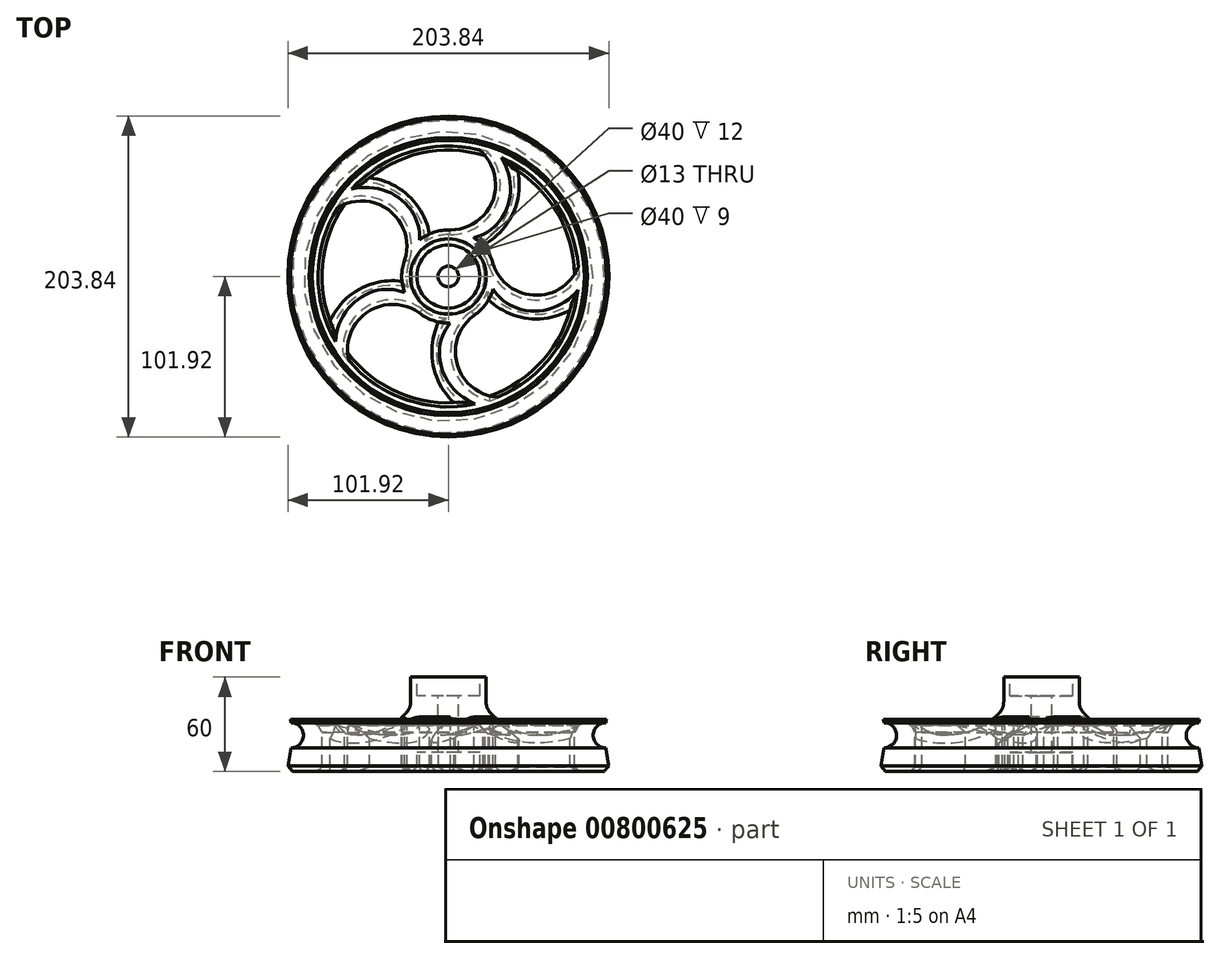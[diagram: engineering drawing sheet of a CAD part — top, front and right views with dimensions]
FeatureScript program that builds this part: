
annotation { "Feature Type Name" : "Feature", "Feature Type Description" : "" }
export const myFeature = defineFeature(function(context is Context, id is Id, definition is map)
    precondition{}
    {
        {
            var Q0;
            Q0=qCreatedBy(makeId("Front.planeOp"),FACE);
            var sketch = newSketch(context, id + "F0", { "sketchPlane" : qUnion([Q0])});
            skArc(sketch, "E0", {"start": v(100, 8) * mm, "mid": v(92, 0) * mm, "end": v(100, -8) * mm});
            skLineSegment(sketch, "E1", {"start": v(125.58, -23) * mm, "end": v(0, -23) * mm, "construction": true});
            skLineSegment(sketch, "E2", {"start": v(102.5, -11.93) * mm, "end": v(102.5, -49.99) * mm, "construction": true});
            skLineSegment(sketch, "E3", {"start": v(100, -8) * mm, "end": v(102.5, -23) * mm});
            skLineSegment(sketch, "E4.MirrorCS", {"start": v(100, 8) * mm, "end": v(100.33, 10) * mm});
            skPoint(sketch, "E5.orphan", {"position": v(102.5, 23) * mm});
            skLineSegment(sketch, "E6", {"start": v(102.5, -23) * mm, "end": v(92.5, -23) * mm});
            skArc(sketch, "E7", {"start": v(88.37, 10) * mm, "mid": v(87.38, 9.33) * mm, "end": v(86.46, 8.57) * mm});
            skLineSegment(sketch, "E8", {"start": v(100.33, 10) * mm, "end": v(88.37, 10) * mm});
            skLineSegment(sketch, "E9", {"start": v(0, 37) * mm, "end": v(98, 37) * mm, "construction": true});
            skLineSegment(sketch, "E10", {"start": v(20, 37) * mm, "end": v(20, 25) * mm});
            skLineSegment(sketch, "E11", {"start": v(20, 25) * mm, "end": v(6.5, 25) * mm});
            skLineSegment(sketch, "E12", {"start": v(6.5, 25) * mm, "end": v(6.5, -11) * mm});
            skLineSegment(sketch, "E13", {"start": v(6.5, -11) * mm, "end": v(20, -11) * mm});
            skLineSegment(sketch, "E14", {"start": v(20, 37) * mm, "end": v(0, 37) * mm});
            skLineSegment(sketch, "E15", {"start": v(0, -23) * mm, "end": v(20, -23) * mm});
            skLineSegment(sketch, "E16.trimOffspring", {"start": v(20, -11) * mm, "end": v(20, -23) * mm});
            skLineSegment(sketch, "E17", {"start": v(20, 37) * mm, "end": v(24, 37) * mm});
            skLineSegment(sketch, "E18", {"start": v(24, 37) * mm, "end": v(24, 17.35) * mm});
            skLineSegment(sketch, "E19", {"start": v(24, -23) * mm, "end": v(20, -23) * mm});
            skLineSegment(sketch, "E20", {"start": v(24, -23) * mm, "end": v(92.5, -23) * mm});
            skArc(sketch, "E21", {"start": v(24, 17.35) * mm, "mid": v(54.67, 0.42) * mm, "end": v(88.37, 10) * mm});
            skLineSegment(sketch, "E22", {"start": v(0, 51.8) * mm, "end": v(0, -76.47) * mm, "construction": true});
            skSolve(sketch);
        }
        {
            var Q0;
            Q0 = qSketchRegion(id + "F0", true);
            var Q1;
            Q1=sQuery(id+"F0.wireOp",EDGE,"E22");
            revolve(context, id + "F1", {"surfaceOperationType" : NewSurfaceOperationType.NEW, "entities" : qUnion([Q0]), "axis" : qUnion([Q1]), "revolveType" : RevolveType.FULL});
        }
        {
            var Q0;
            Q0=makeQuery(id+"F1.opRevolve","SWEPT_FACE",FACE,{"disambiguationData":[OSD([sQuery(id+"F0.wireOp",EDGE,"E17")])]});
            var sketch = newSketch(context, id + "F2", { "sketchPlane" : qUnion([Q0])});
            skCircle(sketch, "E23", {"center": v(0, 0) * mm, "radius": 29.57 * mm});
            skCircle(sketch, "E24", {"center": v(0, 0) * mm, "radius": 80.24 * mm});
            skArc(sketch, "E25", {"start": v(0, 29.57) * mm, "mid": v(27.05, 45.57) * mm, "end": v(23.32, 76.77) * mm});
            skArc(sketch, "E26.0", {"start": v(22, 19.77) * mm, "mid": v(40.88, 39.72) * mm, "end": v(44.15, 67) * mm});
            skArc(sketch, "E27.1.0", {"start": v(-28.12, 9.14) * mm, "mid": v(-34.98, 39.8) * mm, "end": v(-65.81, 45.9) * mm});
            skArc(sketch, "E27.1.1", {"start": v(-12, 27.02) * mm, "mid": v(-25.14, 51.15) * mm, "end": v(-50.07, 62.7) * mm});
            skArc(sketch, "E27.2.0", {"start": v(-17.38, -23.92) * mm, "mid": v(-48.67, -20.97) * mm, "end": v(-64, -48.4) * mm});
            skArc(sketch, "E27.2.1", {"start": v(-29.41, -3.06) * mm, "mid": v(-56.42, -8.1) * mm, "end": v(-75.1, -28.25) * mm});
            skArc(sketch, "E27.3.0", {"start": v(17.38, -23.92) * mm, "mid": v(4.9, -52.77) * mm, "end": v(26.26, -75.82) * mm});
            skArc(sketch, "E27.3.1", {"start": v(-6.17, -28.92) * mm, "mid": v(-9.73, -56.16) * mm, "end": v(3.66, -80.15) * mm});
            skArc(sketch, "E27.4.0", {"start": v(28.12, 9.14) * mm, "mid": v(51.7, -11.64) * mm, "end": v(80.22, 1.55) * mm});
            skArc(sketch, "E27.4.1", {"start": v(25.6, -14.8) * mm, "mid": v(50.4, -26.6) * mm, "end": v(77.36, -21.3) * mm});
            skSolve(sketch);
        }
        {
            var Q0;
            {var subQ6=sQuery(id+"F2.wireOp",EDGE,"E27.2.1");Q0=makeQuery(id+"F2.imprint","IMPRINT",FACE,{"disambiguationData":[TD([[makeQuery(id+"F2.imprint","IMPRINT",EDGE,{"derivedFrom":subQ6}),-1.0]])]});}
            var Q1;
            {var subQ6=sQuery(id+"F2.wireOp",EDGE,"E27.1.1");Q1=makeQuery(id+"F2.imprint","IMPRINT",FACE,{"disambiguationData":[TD([[makeQuery(id+"F2.imprint","IMPRINT",EDGE,{"derivedFrom":subQ6}),-1.0]])]});}
            var Q2;
            {var subQ0=sQuery(id+"F2.wireOp",EDGE,"E26.0");Q2=makeQuery(id+"F2.imprint","IMPRINT",FACE,{"disambiguationData":[TD([[makeQuery(id+"F2.imprint","IMPRINT",EDGE,{"derivedFrom":subQ0}),-1.0]])]});}
            var Q3;
            {var subQ6=sQuery(id+"F2.wireOp",EDGE,"E27.4.1");Q3=makeQuery(id+"F2.imprint","IMPRINT",FACE,{"disambiguationData":[TD([[makeQuery(id+"F2.imprint","IMPRINT",EDGE,{"derivedFrom":subQ6}),-1.0]])]});}
            var Q4;
            {var subQ5=sQuery(id+"F2.wireOp",EDGE,"E27.3.1");Q4=makeQuery(id+"F2.imprint","IMPRINT",FACE,{"disambiguationData":[TD([[makeQuery(id+"F2.imprint","IMPRINT",EDGE,{"derivedFrom":subQ5}),-1.0]])]});}
            extrude(context, id + "F3", {"entities" : qUnion([Q0, Q1, Q2, Q3, Q4]), "operationType" : NewBodyOperationType.REMOVE, "endBound" : BoundingType.THROUGH_ALL, "oppositeDirection" : true, "depth" : 25 * mm, "offsetDistance" : 25 * mm});
        }
        {
            var Q0;
            Q0=makeQuery(id+"F1.opRevolve","SWEPT_FACE",FACE,{"disambiguationData":[OSD([sQuery(id+"F0.wireOp",EDGE,"E6"),sQuery(id+"F0.wireOp",EDGE,"E19"),sQuery(id+"F0.wireOp",EDGE,"E20")])]});
            chamfer(context, id + "F4", {"entities" : qUnion([Q0]), "width" : 3 * mm, "tangentPropagation" : true});
        }
        {
            var Q0;
            {var subQ0=sQuery(id+"F2.wireOp",EDGE,"E24");Q0=makeQuery(id+"F3.boolean.opBoolean","INTERSECT",EDGE,{"derivedFrom":[makeQuery(id+"F1.opRevolve","SWEPT_FACE",FACE,{"disambiguationData":[OSD([sQuery(id+"F0.wireOp",EDGE,"E21")])]}),makeQuery(id+"F3.opExtrude","SWEPT_FACE",FACE,{"disambiguationData":[OSD([subQ0]),TDD([makeQuery(id+"F2.imprint","IMPRINT",EDGE,{"disambiguationData":[TD([[makeQuery(id+"F2.imprint","INTERSECT",VERTEX,{"derivedFrom":[subQ0,sQuery(id+"F2.wireOp",EDGE,"E25")]}),-1.0]])],"derivedFrom":subQ0})])]})]});}
            var Q1;
            {var subQ0=sQuery(id+"F2.wireOp",EDGE,"E24");Q1=makeQuery(id+"F3.boolean.opBoolean","INTERSECT",EDGE,{"derivedFrom":[makeQuery(id+"F1.opRevolve","SWEPT_FACE",FACE,{"disambiguationData":[OSD([sQuery(id+"F0.wireOp",EDGE,"E21")])]}),makeQuery(id+"F3.opExtrude","SWEPT_FACE",FACE,{"disambiguationData":[OSD([subQ0]),TDD([makeQuery(id+"F2.imprint","IMPRINT",EDGE,{"disambiguationData":[TD([[makeQuery(id+"F2.imprint","INTERSECT",VERTEX,{"derivedFrom":[subQ0,sQuery(id+"F2.wireOp",EDGE,"E26.0")]}),1.0]])],"derivedFrom":subQ0})])]})]});}
            var Q2;
            {var subQ0=sQuery(id+"F2.wireOp",EDGE,"E24");Q2=makeQuery(id+"F3.boolean.opBoolean","INTERSECT",EDGE,{"derivedFrom":[makeQuery(id+"F1.opRevolve","SWEPT_FACE",FACE,{"disambiguationData":[OSD([sQuery(id+"F0.wireOp",EDGE,"E21")])]}),makeQuery(id+"F3.opExtrude","SWEPT_FACE",FACE,{"disambiguationData":[OSD([subQ0]),TDD([makeQuery(id+"F2.imprint","IMPRINT",EDGE,{"disambiguationData":[TD([[makeQuery(id+"F2.imprint","INTERSECT",VERTEX,{"derivedFrom":[subQ0,sQuery(id+"F2.wireOp",EDGE,"E27.3.0")]}),-1.0]])],"derivedFrom":subQ0})])]})]});}
            var Q3;
            {var subQ0=sQuery(id+"F2.wireOp",EDGE,"E24");Q3=makeQuery(id+"F3.boolean.opBoolean","INTERSECT",EDGE,{"derivedFrom":[makeQuery(id+"F1.opRevolve","SWEPT_FACE",FACE,{"disambiguationData":[OSD([sQuery(id+"F0.wireOp",EDGE,"E21")])]}),makeQuery(id+"F3.opExtrude","SWEPT_FACE",FACE,{"disambiguationData":[OSD([subQ0]),TDD([makeQuery(id+"F2.imprint","IMPRINT",EDGE,{"disambiguationData":[TD([[makeQuery(id+"F2.imprint","INTERSECT",VERTEX,{"derivedFrom":[subQ0,sQuery(id+"F2.wireOp",EDGE,"E27.2.0")]}),-1.0]])],"derivedFrom":subQ0})])]})]});}
            var Q4;
            {var subQ0=sQuery(id+"F2.wireOp",EDGE,"E24");Q4=makeQuery(id+"F3.boolean.opBoolean","INTERSECT",EDGE,{"derivedFrom":[makeQuery(id+"F1.opRevolve","SWEPT_FACE",FACE,{"disambiguationData":[OSD([sQuery(id+"F0.wireOp",EDGE,"E21")])]}),makeQuery(id+"F3.opExtrude","SWEPT_FACE",FACE,{"disambiguationData":[OSD([subQ0]),TDD([makeQuery(id+"F2.imprint","IMPRINT",EDGE,{"disambiguationData":[TD([[makeQuery(id+"F2.imprint","INTERSECT",VERTEX,{"derivedFrom":[subQ0,sQuery(id+"F2.wireOp",EDGE,"E27.1.0")]}),-1.0]])],"derivedFrom":subQ0})])]})]});}
            var Q5;
            Q5=makeQuery(id+"F3.boolean.opBoolean","INTERSECT",EDGE,{"derivedFrom":[makeQuery(id+"F1.opRevolve","SWEPT_FACE",FACE,{"disambiguationData":[OSD([sQuery(id+"F0.wireOp",EDGE,"E21")])]}),makeQuery(id+"F3.opExtrude","SWEPT_FACE",FACE,{"disambiguationData":[OSD([sQuery(id+"F2.wireOp",EDGE,"E27.1.1")])]})]});
            var Q6;
            Q6=makeQuery(id+"F3.boolean.opBoolean","INTERSECT",EDGE,{"derivedFrom":[makeQuery(id+"F1.opRevolve","SWEPT_FACE",FACE,{"disambiguationData":[OSD([sQuery(id+"F0.wireOp",EDGE,"E21")])]}),makeQuery(id+"F3.opExtrude","SWEPT_FACE",FACE,{"disambiguationData":[OSD([sQuery(id+"F2.wireOp",EDGE,"E26.0")])]})]});
            var Q7;
            Q7=makeQuery(id+"F3.boolean.opBoolean","INTERSECT",EDGE,{"derivedFrom":[makeQuery(id+"F1.opRevolve","SWEPT_FACE",FACE,{"disambiguationData":[OSD([sQuery(id+"F0.wireOp",EDGE,"E21")])]}),makeQuery(id+"F3.opExtrude","SWEPT_FACE",FACE,{"disambiguationData":[OSD([sQuery(id+"F2.wireOp",EDGE,"E27.4.1")])]})]});
            var Q8;
            Q8=makeQuery(id+"F3.boolean.opBoolean","INTERSECT",EDGE,{"derivedFrom":[makeQuery(id+"F1.opRevolve","SWEPT_FACE",FACE,{"disambiguationData":[OSD([sQuery(id+"F0.wireOp",EDGE,"E21")])]}),makeQuery(id+"F3.opExtrude","SWEPT_FACE",FACE,{"disambiguationData":[OSD([sQuery(id+"F2.wireOp",EDGE,"E27.3.1")])]})]});
            var Q9;
            Q9=makeQuery(id+"F3.boolean.opBoolean","INTERSECT",EDGE,{"derivedFrom":[makeQuery(id+"F1.opRevolve","SWEPT_FACE",FACE,{"disambiguationData":[OSD([sQuery(id+"F0.wireOp",EDGE,"E21")])]}),makeQuery(id+"F3.opExtrude","SWEPT_FACE",FACE,{"disambiguationData":[OSD([sQuery(id+"F2.wireOp",EDGE,"E27.2.1")])]})]});
            chamfer(context, id + "F5", {"entities" : qUnion([Q0, Q1, Q2, Q3, Q4, Q5, Q6, Q7, Q8, Q9]), "width" : 5 * mm, "tangentPropagation" : true});
        }
        {
            var Q0;
            Q0=makeQuery(id+"F1.opRevolve","SWEPT_EDGE",EDGE,{"disambiguationData":[OSD([sQuery(id+"F0.wireOp",EDGE,"E18"),sQuery(id+"F0.wireOp",EDGE,"E21")])]});
            fillet(context, id + "F6", {"entities" : qUnion([Q0]), "radius" : 10 * mm, "tangentPropagation" : true, "allowEdgeOverflow" : false});
        }
    });
